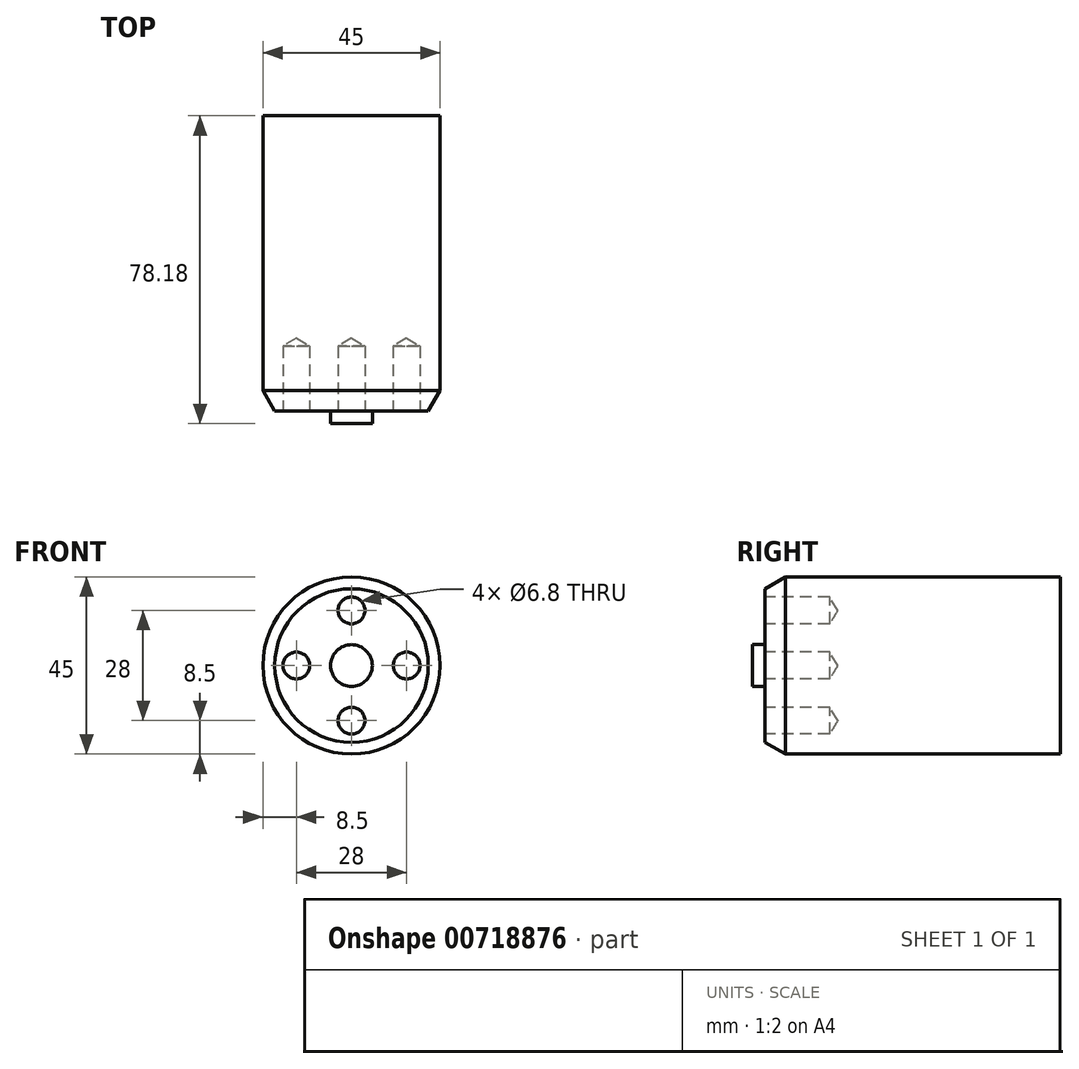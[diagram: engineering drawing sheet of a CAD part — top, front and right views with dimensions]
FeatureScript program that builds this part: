
annotation { "Feature Type Name" : "Feature", "Feature Type Description" : "" }
export const myFeature = defineFeature(function(context is Context, id is Id, definition is map)
    precondition{}
    {
        {
            var Q0;
            Q0=qCreatedBy(makeId("Front.planeOp"),FACE);
            var sketch = newSketch(context, id + "F0", { "sketchPlane" : qUnion([Q0])});
            skCircle(sketch, "E0", {"center": v(0, 0) * mm, "radius": 22.5 * mm});
            skSolve(sketch);
        }
        {
            var Q0;
            Q0 = qSketchRegion(id + "F0", true);
            var Q1;
            Q1=sQuery(id+"F0.wireOp",EDGE,"E0");
            extrude(context, id + "F1", {"entities" : qUnion([Q0]), "surfaceEntities" : qUnion([Q1]), "oppositeDirection" : true, "depth" : 75 * mm, "offsetDistance" : 25.4 * mm});
        }
        {
            var Q0;
            Q0=makeQuery(id+"F1.opExtrude","CAP_FACE",FACE,{"disambiguationData":[OSD([sQuery(id+"F0.wireOp",EDGE,"E0")])],"isStart":true});
            var sketch = newSketch(context, id + "F2", { "sketchPlane" : qUnion([Q0])});
            skCircle(sketch, "E1", {"center": v(0, 0) * mm, "radius": 14 * mm, "construction": true});
            skPoint(sketch, "E2", {"position": v(0, 14) * mm});
            skPoint(sketch, "E3", {"position": v(14, 0) * mm});
            skPoint(sketch, "E4", {"position": v(0, -14) * mm});
            skPoint(sketch, "E5", {"position": v(-14, 0) * mm});
            skSolve(sketch);
        }
        {
            var Q0;
            Q0=sQuery(id+"F2.wireOp",VERTEX,"E4");
            var Q1;
            Q1=sQuery(id+"F2.wireOp",VERTEX,"E3");
            var Q2;
            Q2=sQuery(id+"F2.wireOp",VERTEX,"E2");
            var Q3;
            Q3=sQuery(id+"F2.wireOp",VERTEX,"E5");
            var Q4;
            Q4=makeQuery(id+"F1.opExtrude","SWEPT_BODY",BODY,{"disambiguationData":[OSD([sQuery(id+"F0.wireOp",EDGE,"E0")])]});
            hole(context, id + "F3", {"style" : HoleStyle.SIMPLE, "endStyle" : HoleEndStyle.BLIND, "standardTappedOrClearance" : lookupTablePath({ "standard" : "ISO", "engagement" : "75%", "pitch" : "1.25 mm", "size" : "M8", "type" : "Tapped" }), "standardBlindInLast" : lookupTablePath({ "standard" : "ISO", "engagement" : "75%", "pitch" : "1.25 mm", "size" : "M8", "type" : "Tapped" }), "holeDiameter" : 6.8 * mm, "majorDiameter" : 8 * mm, "showTappedDepth" : true, "holeDepth" : 16.45 * mm, "isTappedThrough" : true, "tappedDepth" : 12.7 * mm, "tapClearance" : 3, "locations" : qUnion([Q0, Q1, Q2, Q3]), "scope" : qUnion([Q4])});
        }
        {
            var Q0;
            Q0=makeQuery(id+"F1.opExtrude","CAP_FACE",FACE,{"disambiguationData":[OSD([sQuery(id+"F0.wireOp",EDGE,"E0")])],"isStart":true});
            var sketch = newSketch(context, id + "F4", { "sketchPlane" : qUnion([Q0])});
            skCircle(sketch, "E6", {"center": v(0, 0) * mm, "radius": 5.29 * mm});
            skSolve(sketch);
        }
        {
            var Q0;
            Q0 = qSketchRegion(id + "F4", true);
            extrude(context, id + "F5", {"entities" : qUnion([Q0]), "operationType" : NewBodyOperationType.ADD, "depth" : 3.17 * mm, "offsetDistance" : 25.4 * mm});
        }
        {
            var Q0;
            Q0=makeQuery(id+"F1.opExtrude","CAP_EDGE",EDGE,{"disambiguationData":[OSD([sQuery(id+"F0.wireOp",EDGE,"E0")])],"isStart":true});
            chamfer(context, id + "F6", {"entities" : qUnion([Q0]), "chamferType" : ChamferType.OFFSET_ANGLE, "width" : 3 * mm, "oppositeDirection" : false, "angle" : 60 * degree, "tangentPropagation" : true});
        }
    });
